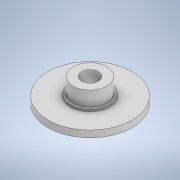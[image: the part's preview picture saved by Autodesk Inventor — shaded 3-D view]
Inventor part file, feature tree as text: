
AUTODESK INVENTOR PART (.ipt)
format: ipt  version: 2022 (Build 260153000, 153)  size: 122,880 bytes
history: native  units: mm
features: extrude x3, sketch x3
ambient origin geometry x8: Origin, YZ Plane, XZ Plane, XY Plane, X Axis, Y Axis, Z Axis, Center Point
bodies: Solid1 (feature_tree)
feature tree (6):
  extrude  "Extrusion1"  Depth=20.0mm TaperAngle=0.0deg
  extrude  "Extrusion2"  Depth=50.0mm TaperAngle=0.0deg
  extrude  "Extrusion3"  Depth=6.0mm
  sketch  "Sketch1"  dims[d0=250.0mm d1=20.0mm d2=0.0mm]
  sketch  "Sketch2"  dims[d3=50.0mm d4=50.0mm d5=0.0mm]
  sketch  "Sketch3"  dims[d6=8.0mm d7=116.0mm d8=6.0mm d9=0.0mm d10=100.0mm]
